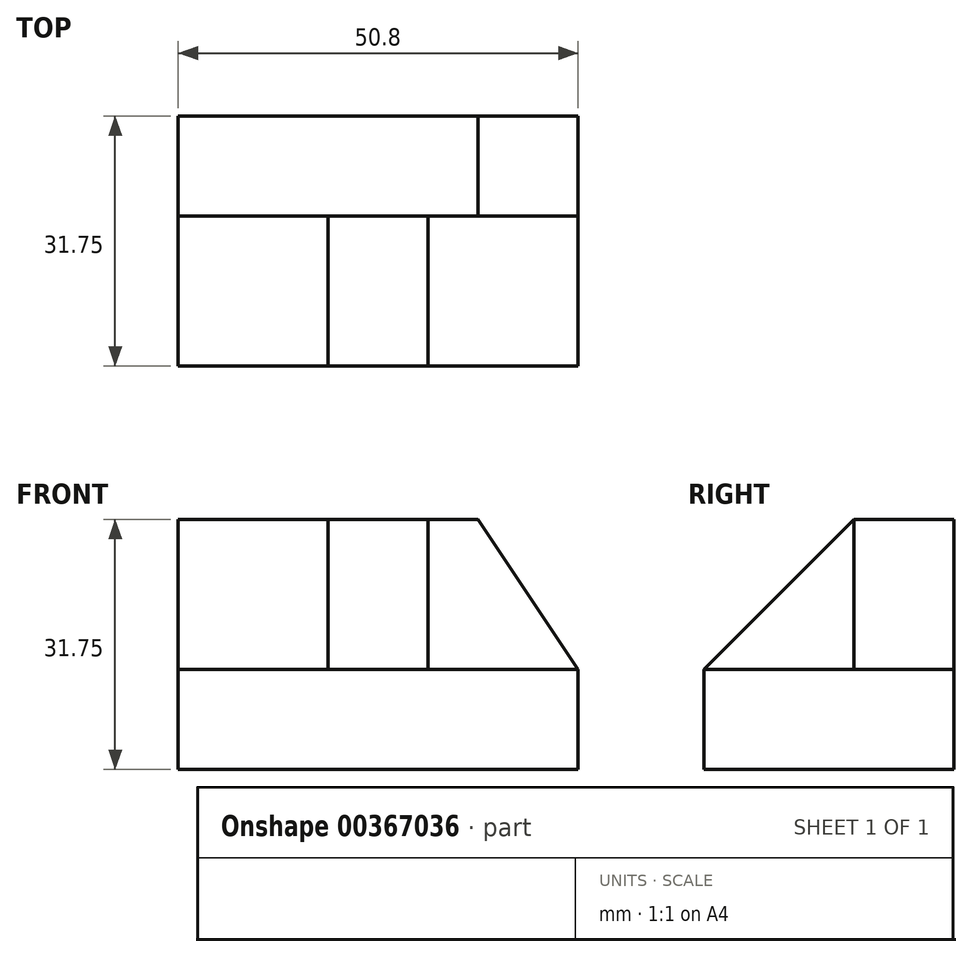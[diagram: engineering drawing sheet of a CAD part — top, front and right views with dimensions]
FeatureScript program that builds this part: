
annotation { "Feature Type Name" : "Feature", "Feature Type Description" : "" }
export const myFeature = defineFeature(function(context is Context, id is Id, definition is map)
    precondition{}
    {
        {
            var Q0;
            Q0=qCreatedBy(makeId("Top.planeOp"),FACE);
            var sketch = newSketch(context, id + "F0", { "sketchPlane" : qUnion([Q0])});
            skLineSegment(sketch, "E0", {"start": v(0, 0) * mm, "end": v(50.8, 0) * mm});
            skLineSegment(sketch, "E1", {"start": v(50.8, 0) * mm, "end": v(50.8, 31.75) * mm});
            skLineSegment(sketch, "E2", {"start": v(50.8, 31.75) * mm, "end": v(0, 31.75) * mm});
            skLineSegment(sketch, "E3", {"start": v(0, 31.75) * mm, "end": v(0, 0) * mm});
            skSolve(sketch);
        }
        {
            var Q0;
            Q0 = qSketchRegion(id + "F0", true);
            extrude(context, id + "F1", {"entities" : qUnion([Q0]), "depth" : 31.75 * mm});
        }
        {
            var Q0;
            Q0=makeQuery(id+"F1.opExtrude","CAP_FACE",FACE,{"disambiguationData":[OSD([sQuery(id+"F0.wireOp",EDGE,"E0"),sQuery(id+"F0.wireOp",EDGE,"E1"),sQuery(id+"F0.wireOp",EDGE,"E2"),sQuery(id+"F0.wireOp",EDGE,"E3")])],"isStart":false});
            var sketch = newSketch(context, id + "F2", { "sketchPlane" : qUnion([Q0])});
            skLineSegment(sketch, "E4", {"start": v(50.8, 19.05) * mm, "end": v(31.75, 19.05) * mm});
            skLineSegment(sketch, "E5", {"start": v(31.75, 19.05) * mm, "end": v(31.75, 0) * mm});
            skLineSegment(sketch, "E6", {"start": v(0, 19.05) * mm, "end": v(19.05, 19.05) * mm});
            skLineSegment(sketch, "E7", {"start": v(19.05, 19.05) * mm, "end": v(19.05, 0) * mm});
            skSolve(sketch);
        }
        {
            var Q0;
            {var subQ0=sQuery(id+"F2.wireOp",EDGE,"E4");Q0=makeQuery(id+"F2.imprint","IMPRINT",FACE,{"disambiguationData":[TD([[makeQuery(id+"F2.imprint","IMPRINT",EDGE,{"derivedFrom":subQ0}),1.0]])]});}
            var Q1;
            {var subQ0=sQuery(id+"F2.wireOp",EDGE,"E6");Q1=makeQuery(id+"F2.imprint","IMPRINT",FACE,{"disambiguationData":[TD([[makeQuery(id+"F2.imprint","IMPRINT",EDGE,{"derivedFrom":subQ0}),-1.0]])]});}
            extrude(context, id + "F3", {"entities" : qUnion([Q0, Q1]), "operationType" : NewBodyOperationType.REMOVE, "oppositeDirection" : true, "depth" : 19.05 * mm});
        }
        {
            var Q0;
            Q0=makeQuery(id+"F3.boolean.opBoolean","COPY",FACE,{"derivedFrom":makeQuery(id+"F3.opExtrude","SWEPT_FACE",FACE,{"disambiguationData":[OSD([sQuery(id+"F2.wireOp",EDGE,"E4")])]})});
            var sketch = newSketch(context, id + "F4", { "sketchPlane" : qUnion([Q0])});
            skLineSegment(sketch, "E8", {"start": v(38.1, 31.75) * mm, "end": v(50.8, 12.7) * mm});
            skSolve(sketch);
        }
        {
            var Q0;
            Q0=makeQuery(id+"F3.boolean.opBoolean","COPY",FACE,{"derivedFrom":makeQuery(id+"F3.opExtrude","SWEPT_FACE",FACE,{"disambiguationData":[OSD([sQuery(id+"F2.wireOp",EDGE,"E5")])]})});
            var sketch = newSketch(context, id + "F5", { "sketchPlane" : qUnion([Q0])});
            skLineSegment(sketch, "E9", {"start": v(19.05, 31.75) * mm, "end": v(0, 12.7) * mm});
            skSolve(sketch);
        }
        {
            var Q0;
            Q0=makeQuery(id+"F5.imprint","IMPRINT",FACE,{"disambiguationData":[TD([[makeQuery(id+"F5.imprint","IMPRINT",EDGE,{"derivedFrom":sQuery(id+"F5.wireOp",EDGE,"E9")}),-1.0]])]});
            extrude(context, id + "F6", {"entities" : qUnion([Q0]), "operationType" : NewBodyOperationType.REMOVE, "oppositeDirection" : true, "depth" : 25.4 * mm});
        }
        {
            var Q0;
            {var subQ0=sQuery(id+"F4.wireOp",EDGE,"E8");Q0=makeQuery(id+"F4.imprint","IMPRINT",FACE,{"disambiguationData":[TD([[makeQuery(id+"F4.imprint","IMPRINT",EDGE,{"derivedFrom":subQ0}),1.0]])]});}
            extrude(context, id + "F7", {"entities" : qUnion([Q0]), "operationType" : NewBodyOperationType.REMOVE, "oppositeDirection" : true, "depth" : 25.4 * mm});
        }
    });
